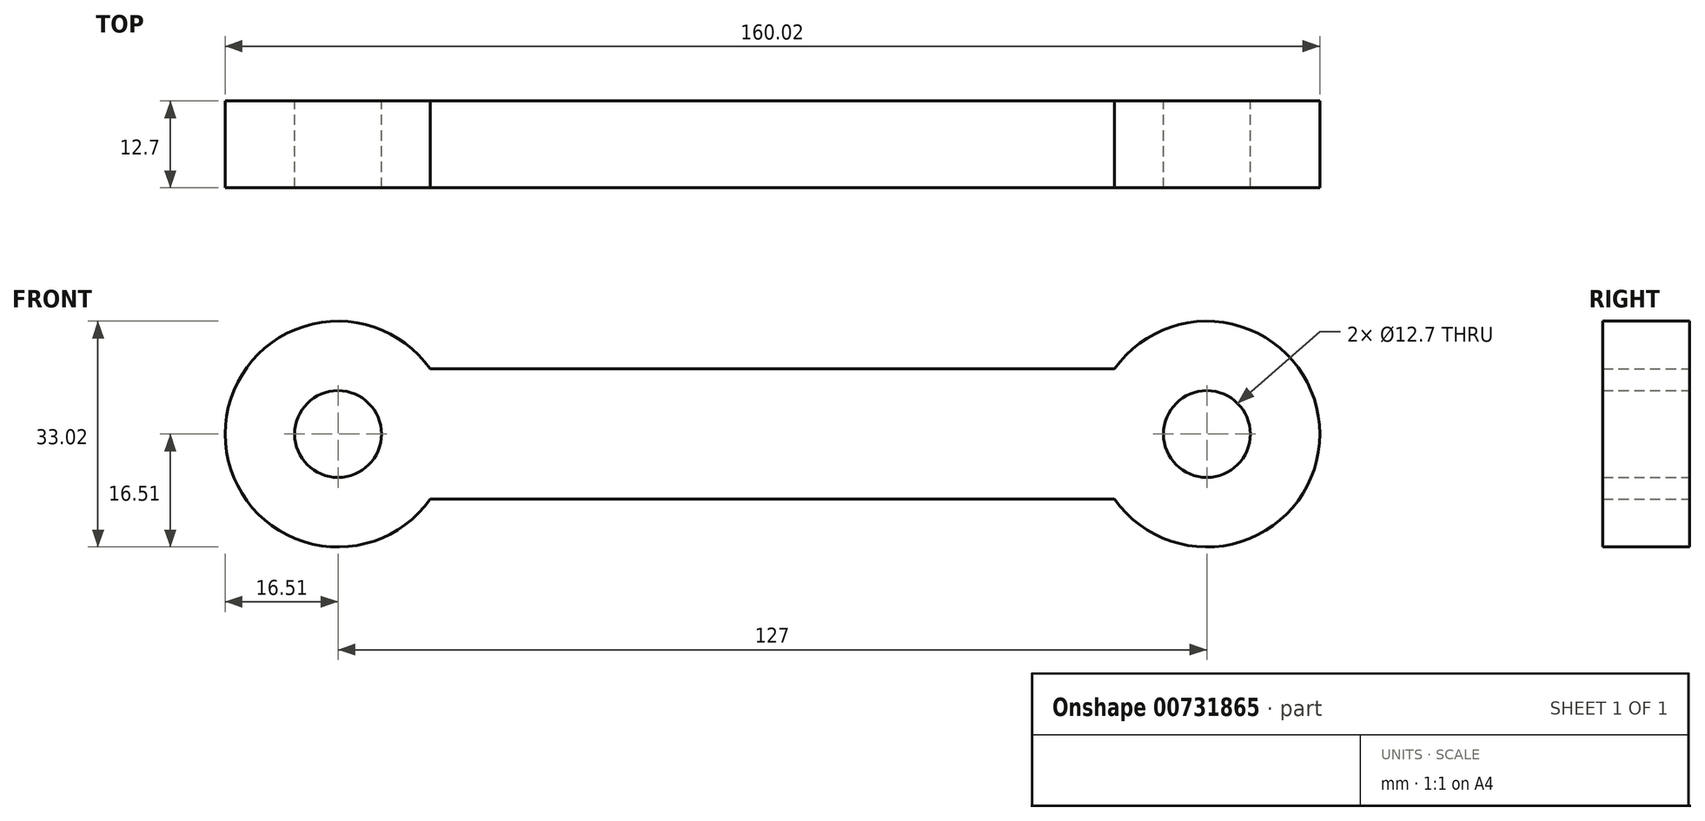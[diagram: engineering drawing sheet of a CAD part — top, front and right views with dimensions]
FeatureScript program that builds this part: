
annotation { "Feature Type Name" : "Feature", "Feature Type Description" : "" }
export const myFeature = defineFeature(function(context is Context, id is Id, definition is map)
    precondition{}
    {
        {
            var Q0;
            Q0=qCreatedBy(makeId("Front.planeOp"),FACE);
            var sketch = newSketch(context, id + "F0", { "sketchPlane" : qUnion([Q0])});
            skLineSegment(sketch, "E0.bottom", {"start": v(63.5, -9.53) * mm, "end": v(-63.5, -9.52) * mm});
            skLineSegment(sketch, "E0.top", {"start": v(63.5, 9.52) * mm, "end": v(-63.5, 9.53) * mm});
            skLineSegment(sketch, "E0.left", {"start": v(63.5, -9.53) * mm, "end": v(63.5, 9.52) * mm});
            skLineSegment(sketch, "E0.right", {"start": v(-63.5, -9.52) * mm, "end": v(-63.5, 9.53) * mm});
            skPoint(sketch, "E0.middle", {"position": v(0, 0) * mm});
            skCircle(sketch, "E1", {"center": v(-63.5, 0) * mm, "radius": 16.51 * mm});
            skCircle(sketch, "E2.MirrorC", {"center": v(63.5, 0) * mm, "radius": 16.51 * mm});
            skCircle(sketch, "E3", {"center": v(-63.5, 0) * mm, "radius": 6.35 * mm});
            skCircle(sketch, "E4.MirrorC", {"center": v(63.5, 0) * mm, "radius": 6.35 * mm});
            skSolve(sketch);
        }
        {
            var Q0;
            Q0 = qSketchRegion(id + "F0", true);
            extrude(context, id + "F1", {"entities" : qUnion([Q0]), "endBound" : BoundingType.SYMMETRIC, "depth" : 12.7 * mm, "offsetDistance" : 25.4 * mm});
        }
    });
